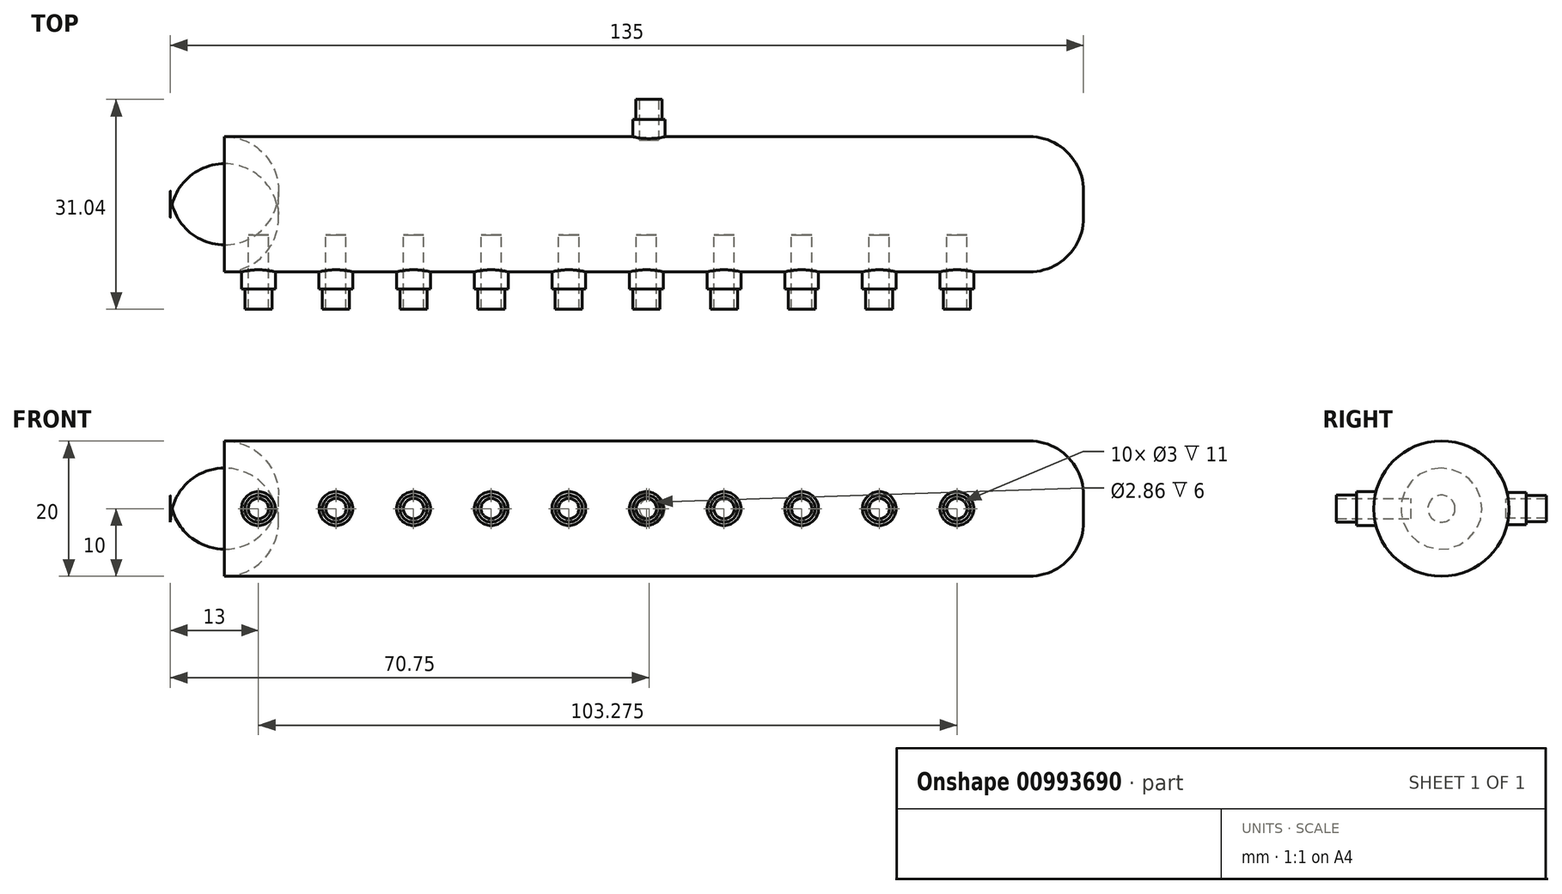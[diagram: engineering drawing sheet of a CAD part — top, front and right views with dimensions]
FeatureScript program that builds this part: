
annotation { "Feature Type Name" : "Feature", "Feature Type Description" : "" }
export const myFeature = defineFeature(function(context is Context, id is Id, definition is map)
    precondition{}
    {
        {
            assignVariable(context, id + "F0", {"name" : "big_radius", "anyValue" : 20});
        }
        {
            assignVariable(context, id + "F1", {"name" : "tube_length", "anyValue" : 135});
        }
        {
            var Q0;
            Q0=qCreatedBy(makeId("Right.planeOp"),FACE);
            var sketch = newSketch(context, id + "F2", { "sketchPlane" : qUnion([Q0])});
            skCircle(sketch, "E0", {"center": v(0, 0) * mm, "radius": 10 * mm});
            skLineSegment(sketch, "E1", {"start": v(-10, 0) * mm, "end": v(-10, 26.48) * mm, "construction": true});
            skSolve(sketch);
        }
        {
            var Q0;
            Q0=makeQuery(id+"F2.imprint","IMPRINT",FACE,{"disambiguationData":[TD([[makeQuery(id+"F2.imprint","IMPRINT",EDGE,{"derivedFrom":sQuery(id+"F2.wireOp",EDGE,"E0")}),1.0]])]});
            extrude(context, id + "F3", {"entities" : qUnion([Q0]), "depth" : (getVariable(context, 'tube_length')) * mm, "offsetDistance" : 25 * mm});
        }
        {
            var Q0;
            Q0=makeQuery(id+"F3.opExtrude","CAP_FACE",FACE,{"disambiguationData":[OSD([sQuery(id+"F2.wireOp",EDGE,"E0")])],"isStart":false});
            fillet(context, id + "F4", {"entities" : qUnion([Q0]), "radius" : 8 * mm, "tangentPropagation" : true, "allowEdgeOverflow" : false});
        }
        {
            var Q0;
            Q0=makeQuery(id+"F3.opExtrude","CAP_FACE",FACE,{"disambiguationData":[OSD([sQuery(id+"F2.wireOp",EDGE,"E0")])],"isStart":true});
            fillet(context, id + "F5", {"entities" : qUnion([Q0]), "radius" : 8 * mm, "tangentPropagation" : true, "allowEdgeOverflow" : false});
        }
        {
            var Q0;
            Q0=qCreatedBy(makeId("Front.planeOp"),FACE);
            cPlane(context, id + "F6", {"entities" : qUnion([Q0]), "cplaneType" : CPlaneType.OFFSET, "offset" : (getVariable(context, 'big_radius') / 2.1) * mm, "width" : 150 * mm, "height" : 150 * mm});
        }
        {
            var Q0;
            Q0=qCreatedBy(id+"F6.planeOp",FACE);
            var sketch = newSketch(context, id + "F7", { "sketchPlane" : qUnion([Q0])});
            skCircle(sketch, "E2", {"center": v(13, 0) * mm, "radius": 2.5 * mm});
            skCircle(sketch, "E3.0", {"center": v(13, 0) * mm, "radius": 1.5 * mm});
            skCircle(sketch, "E4.1.0.0", {"center": v(24.48, 0) * mm, "radius": 1.5 * mm});
            skCircle(sketch, "E4.1.0.1", {"center": v(24.48, 0) * mm, "radius": 2.5 * mm});
            skCircle(sketch, "E4.2.0.0", {"center": v(35.95, 0) * mm, "radius": 1.5 * mm});
            skCircle(sketch, "E4.2.0.1", {"center": v(35.95, 0) * mm, "radius": 2.5 * mm});
            skCircle(sketch, "E4.3.0.0", {"center": v(47.43, 0) * mm, "radius": 1.5 * mm});
            skCircle(sketch, "E4.3.0.1", {"center": v(47.43, 0) * mm, "radius": 2.5 * mm});
            skCircle(sketch, "E4.4.0.0", {"center": v(58.9, 0) * mm, "radius": 1.5 * mm});
            skCircle(sketch, "E4.4.0.1", {"center": v(58.9, 0) * mm, "radius": 2.5 * mm});
            skCircle(sketch, "E4.5.0.0", {"center": v(70.38, 0) * mm, "radius": 1.5 * mm});
            skCircle(sketch, "E4.5.0.1", {"center": v(70.38, 0) * mm, "radius": 2.5 * mm});
            skCircle(sketch, "E4.6.0.0", {"center": v(81.85, 0) * mm, "radius": 1.5 * mm});
            skCircle(sketch, "E4.6.0.1", {"center": v(81.85, 0) * mm, "radius": 2.5 * mm});
            skCircle(sketch, "E4.7.0.0", {"center": v(93.33, 0) * mm, "radius": 1.5 * mm});
            skCircle(sketch, "E4.7.0.1", {"center": v(93.33, 0) * mm, "radius": 2.5 * mm});
            skCircle(sketch, "E4.8.0.0", {"center": v(104.8, 0) * mm, "radius": 1.5 * mm});
            skCircle(sketch, "E4.8.0.1", {"center": v(104.8, 0) * mm, "radius": 2.5 * mm});
            skCircle(sketch, "E4.9.0.0", {"center": v(116.28, 0) * mm, "radius": 1.5 * mm});
            skCircle(sketch, "E4.9.0.1", {"center": v(116.28, 0) * mm, "radius": 2.5 * mm});
            skLineSegment(sketch, "E4.direction1", {"start": v(13, 0) * mm, "end": v(24.48, 0) * mm, "construction": true});
            skSolve(sketch);
        }
        {
            var Q0;
            Q0=makeQuery(id+"F7.imprint","IMPRINT",FACE,{"disambiguationData":[TD([[makeQuery(id+"F7.imprint","IMPRINT",EDGE,{"derivedFrom":sQuery(id+"F7.wireOp",EDGE,"E2")}),1.0]])]});
            var Q1;
            Q1=makeQuery(id+"F7.imprint","IMPRINT",FACE,{"disambiguationData":[TD([[makeQuery(id+"F7.imprint","IMPRINT",EDGE,{"derivedFrom":sQuery(id+"F7.wireOp",EDGE,"E4.1.0.0")}),-1.0]])]});
            var Q2;
            Q2=makeQuery(id+"F7.imprint","IMPRINT",FACE,{"disambiguationData":[TD([[makeQuery(id+"F7.imprint","IMPRINT",EDGE,{"derivedFrom":sQuery(id+"F7.wireOp",EDGE,"E4.2.0.0")}),-1.0]])]});
            var Q3;
            Q3=makeQuery(id+"F7.imprint","IMPRINT",FACE,{"disambiguationData":[TD([[makeQuery(id+"F7.imprint","IMPRINT",EDGE,{"derivedFrom":sQuery(id+"F7.wireOp",EDGE,"E4.3.0.0")}),-1.0]])]});
            var Q4;
            Q4=makeQuery(id+"F7.imprint","IMPRINT",FACE,{"disambiguationData":[TD([[makeQuery(id+"F7.imprint","IMPRINT",EDGE,{"derivedFrom":sQuery(id+"F7.wireOp",EDGE,"E4.4.0.0")}),-1.0]])]});
            var Q5;
            Q5=makeQuery(id+"F7.imprint","IMPRINT",FACE,{"disambiguationData":[TD([[makeQuery(id+"F7.imprint","IMPRINT",EDGE,{"derivedFrom":sQuery(id+"F7.wireOp",EDGE,"E4.5.0.0")}),-1.0]])]});
            var Q6;
            Q6=makeQuery(id+"F7.imprint","IMPRINT",FACE,{"disambiguationData":[TD([[makeQuery(id+"F7.imprint","IMPRINT",EDGE,{"derivedFrom":sQuery(id+"F7.wireOp",EDGE,"E4.6.0.0")}),-1.0]])]});
            var Q7;
            Q7=makeQuery(id+"F7.imprint","IMPRINT",FACE,{"disambiguationData":[TD([[makeQuery(id+"F7.imprint","IMPRINT",EDGE,{"derivedFrom":sQuery(id+"F7.wireOp",EDGE,"E4.7.0.0")}),-1.0]])]});
            var Q8;
            Q8=makeQuery(id+"F7.imprint","IMPRINT",FACE,{"disambiguationData":[TD([[makeQuery(id+"F7.imprint","IMPRINT",EDGE,{"derivedFrom":sQuery(id+"F7.wireOp",EDGE,"E4.8.0.0")}),-1.0]])]});
            var Q9;
            Q9=makeQuery(id+"F7.imprint","IMPRINT",FACE,{"disambiguationData":[TD([[makeQuery(id+"F7.imprint","IMPRINT",EDGE,{"derivedFrom":sQuery(id+"F7.wireOp",EDGE,"E4.9.0.0")}),-1.0]])]});
            extrude(context, id + "F8", {"entities" : qUnion([Q0, Q1, Q2, Q3, Q4, Q5, Q6, Q7, Q8, Q9]), "operationType" : NewBodyOperationType.ADD, "depth" : 3 * mm, "offsetDistance" : 25 * mm});
        }
        {
            var Q0;
            Q0=makeQuery(id+"F7.imprint","IMPRINT",FACE,{"disambiguationData":[TD([[makeQuery(id+"F7.imprint","IMPRINT",EDGE,{"derivedFrom":sQuery(id+"F7.wireOp",EDGE,"E3.0")}),1.0]])]});
            var Q1;
            Q1=makeQuery(id+"F7.imprint","IMPRINT",FACE,{"disambiguationData":[TD([[makeQuery(id+"F7.imprint","IMPRINT",EDGE,{"derivedFrom":sQuery(id+"F7.wireOp",EDGE,"E4.1.0.0")}),1.0]])]});
            var Q2;
            Q2=makeQuery(id+"F7.imprint","IMPRINT",FACE,{"disambiguationData":[TD([[makeQuery(id+"F7.imprint","IMPRINT",EDGE,{"derivedFrom":sQuery(id+"F7.wireOp",EDGE,"E4.2.0.0")}),1.0]])]});
            var Q3;
            Q3=makeQuery(id+"F7.imprint","IMPRINT",FACE,{"disambiguationData":[TD([[makeQuery(id+"F7.imprint","IMPRINT",EDGE,{"derivedFrom":sQuery(id+"F7.wireOp",EDGE,"E4.3.0.0")}),1.0]])]});
            var Q4;
            Q4=makeQuery(id+"F7.imprint","IMPRINT",FACE,{"disambiguationData":[TD([[makeQuery(id+"F7.imprint","IMPRINT",EDGE,{"derivedFrom":sQuery(id+"F7.wireOp",EDGE,"E4.4.0.0")}),1.0]])]});
            var Q5;
            Q5=makeQuery(id+"F7.imprint","IMPRINT",FACE,{"disambiguationData":[TD([[makeQuery(id+"F7.imprint","IMPRINT",EDGE,{"derivedFrom":sQuery(id+"F7.wireOp",EDGE,"E4.5.0.0")}),1.0]])]});
            var Q6;
            Q6=makeQuery(id+"F7.imprint","IMPRINT",FACE,{"disambiguationData":[TD([[makeQuery(id+"F7.imprint","IMPRINT",EDGE,{"derivedFrom":sQuery(id+"F7.wireOp",EDGE,"E4.6.0.0")}),1.0]])]});
            var Q7;
            Q7=makeQuery(id+"F7.imprint","IMPRINT",FACE,{"disambiguationData":[TD([[makeQuery(id+"F7.imprint","IMPRINT",EDGE,{"derivedFrom":sQuery(id+"F7.wireOp",EDGE,"E4.7.0.0")}),1.0]])]});
            var Q8;
            Q8=makeQuery(id+"F7.imprint","IMPRINT",FACE,{"disambiguationData":[TD([[makeQuery(id+"F7.imprint","IMPRINT",EDGE,{"derivedFrom":sQuery(id+"F7.wireOp",EDGE,"E4.8.0.0")}),1.0]])]});
            var Q9;
            Q9=makeQuery(id+"F7.imprint","IMPRINT",FACE,{"disambiguationData":[TD([[makeQuery(id+"F7.imprint","IMPRINT",EDGE,{"derivedFrom":sQuery(id+"F7.wireOp",EDGE,"E4.9.0.0")}),1.0]])]});
            extrude(context, id + "F9", {"entities" : qUnion([Q0, Q1, Q2, Q3, Q4, Q5, Q6, Q7, Q8, Q9]), "operationType" : NewBodyOperationType.REMOVE, "endBound" : BoundingType.SYMMETRIC, "oppositeDirection" : true, "depth" : 10 * mm, "offsetDistance" : 25 * mm});
        }
        {
            var Q0;
            Q0=qCreatedBy(makeId("Front.planeOp"),FACE);
            cPlane(context, id + "F10", {"entities" : qUnion([Q0]), "cplaneType" : CPlaneType.OFFSET, "offset" : (getVariable(context, 'big_radius') / 2.1) * mm, "oppositeDirection" : true, "width" : 150 * mm, "height" : 150 * mm});
        }
        {
            var Q0;
            Q0=qCreatedBy(id+"F10.planeOp",FACE);
            var sketch = newSketch(context, id + "F11", { "sketchPlane" : qUnion([Q0])});
            skCircle(sketch, "E5.0", {"center": v(70.75, 0) * mm, "radius": 2.38 * mm});
            skCircle(sketch, "E5.1", {"center": v(70.75, 0) * mm, "radius": 1.43 * mm});
            skSolve(sketch);
        }
        {
            var Q0;
            Q0=makeQuery(id+"F11.imprint","IMPRINT",FACE,{"disambiguationData":[TD([[makeQuery(id+"F11.imprint","IMPRINT",EDGE,{"derivedFrom":sQuery(id+"F11.wireOp",EDGE,"E5.1")}),1.0]])]});
            extrude(context, id + "F12", {"entities" : qUnion([Q0]), "operationType" : NewBodyOperationType.REMOVE, "oppositeDirection" : true, "depth" : 10 * mm, "offsetDistance" : 25 * mm});
        }
        {
            var Q0;
            Q0=makeQuery(id+"F11.imprint","IMPRINT",FACE,{"disambiguationData":[TD([[makeQuery(id+"F11.imprint","IMPRINT",EDGE,{"derivedFrom":sQuery(id+"F11.wireOp",EDGE,"E5.0")}),1.0]])]});
            extrude(context, id + "F13", {"entities" : qUnion([Q0]), "operationType" : NewBodyOperationType.ADD, "oppositeDirection" : true, "depth" : 3 * mm, "offsetDistance" : 25 * mm});
        }
        {
            var Q0;
            Q0=makeQuery(id+"F8.opExtrude","CAP_FACE",FACE,{"disambiguationData":[OSD([sQuery(id+"F7.wireOp",EDGE,"E2"),sQuery(id+"F7.wireOp",EDGE,"E3.0")])],"isStart":false});
            var sketch = newSketch(context, id + "F14", { "sketchPlane" : qUnion([Q0])});
            skCircle(sketch, "E6.0", {"center": v(13, 0) * mm, "radius": 1.5 * mm});
            skCircle(sketch, "E7.0", {"center": v(13, 0) * mm, "radius": 2 * mm});
            skCircle(sketch, "E8.1.0.0", {"center": v(24.47, 0) * mm, "radius": 1.5 * mm});
            skCircle(sketch, "E8.1.0.1", {"center": v(24.47, 0) * mm, "radius": 2 * mm});
            skCircle(sketch, "E8.2.0.0", {"center": v(35.95, 0) * mm, "radius": 1.5 * mm});
            skCircle(sketch, "E8.2.0.1", {"center": v(35.95, 0) * mm, "radius": 2 * mm});
            skCircle(sketch, "E8.3.0.0", {"center": v(47.42, 0) * mm, "radius": 1.5 * mm});
            skCircle(sketch, "E8.3.0.1", {"center": v(47.42, 0) * mm, "radius": 2 * mm});
            skCircle(sketch, "E8.4.0.0", {"center": v(58.9, 0) * mm, "radius": 1.5 * mm});
            skCircle(sketch, "E8.4.0.1", {"center": v(58.9, 0) * mm, "radius": 2 * mm});
            skCircle(sketch, "E8.5.0.0", {"center": v(70.38, 0) * mm, "radius": 1.5 * mm});
            skCircle(sketch, "E8.5.0.1", {"center": v(70.38, 0) * mm, "radius": 2 * mm});
            skCircle(sketch, "E8.6.0.0", {"center": v(81.85, 0) * mm, "radius": 1.5 * mm});
            skCircle(sketch, "E8.6.0.1", {"center": v(81.85, 0) * mm, "radius": 2 * mm});
            skCircle(sketch, "E8.7.0.0", {"center": v(93.32, 0) * mm, "radius": 1.5 * mm});
            skCircle(sketch, "E8.7.0.1", {"center": v(93.32, 0) * mm, "radius": 2 * mm});
            skCircle(sketch, "E8.8.0.0", {"center": v(104.8, 0) * mm, "radius": 1.5 * mm});
            skCircle(sketch, "E8.8.0.1", {"center": v(104.8, 0) * mm, "radius": 2 * mm});
            skCircle(sketch, "E8.9.0.0", {"center": v(116.27, 0) * mm, "radius": 1.5 * mm});
            skCircle(sketch, "E8.9.0.1", {"center": v(116.27, 0) * mm, "radius": 2 * mm});
            skLineSegment(sketch, "E8.direction1", {"start": v(13, 0) * mm, "end": v(24.47, 0) * mm, "construction": true});
            skSolve(sketch);
        }
        {
            var Q0;
            Q0=makeQuery(id+"F14.imprint","IMPRINT",FACE,{"disambiguationData":[TD([[makeQuery(id+"F14.imprint","IMPRINT",EDGE,{"derivedFrom":sQuery(id+"F14.wireOp",EDGE,"E6.0")}),-1.0]])]});
            var Q1;
            Q1=makeQuery(id+"F14.imprint","IMPRINT",FACE,{"disambiguationData":[TD([[makeQuery(id+"F14.imprint","IMPRINT",EDGE,{"derivedFrom":sQuery(id+"F14.wireOp",EDGE,"E8.1.0.0")}),-1.0]])]});
            var Q2;
            Q2=makeQuery(id+"F14.imprint","IMPRINT",FACE,{"disambiguationData":[TD([[makeQuery(id+"F14.imprint","IMPRINT",EDGE,{"derivedFrom":sQuery(id+"F14.wireOp",EDGE,"E8.2.0.0")}),-1.0]])]});
            var Q3;
            Q3=makeQuery(id+"F14.imprint","IMPRINT",FACE,{"disambiguationData":[TD([[makeQuery(id+"F14.imprint","IMPRINT",EDGE,{"derivedFrom":sQuery(id+"F14.wireOp",EDGE,"E8.3.0.0")}),-1.0]])]});
            var Q4;
            Q4=makeQuery(id+"F14.imprint","IMPRINT",FACE,{"disambiguationData":[TD([[makeQuery(id+"F14.imprint","IMPRINT",EDGE,{"derivedFrom":sQuery(id+"F14.wireOp",EDGE,"E8.4.0.0")}),-1.0]])]});
            var Q5;
            Q5=makeQuery(id+"F14.imprint","IMPRINT",FACE,{"disambiguationData":[TD([[makeQuery(id+"F14.imprint","IMPRINT",EDGE,{"derivedFrom":sQuery(id+"F14.wireOp",EDGE,"E8.5.0.0")}),-1.0]])]});
            var Q6;
            Q6=makeQuery(id+"F14.imprint","IMPRINT",FACE,{"disambiguationData":[TD([[makeQuery(id+"F14.imprint","IMPRINT",EDGE,{"derivedFrom":sQuery(id+"F14.wireOp",EDGE,"E8.6.0.0")}),-1.0]])]});
            var Q7;
            Q7=makeQuery(id+"F14.imprint","IMPRINT",FACE,{"disambiguationData":[TD([[makeQuery(id+"F14.imprint","IMPRINT",EDGE,{"derivedFrom":sQuery(id+"F14.wireOp",EDGE,"E8.7.0.0")}),-1.0]])]});
            var Q8;
            Q8=makeQuery(id+"F14.imprint","IMPRINT",FACE,{"disambiguationData":[TD([[makeQuery(id+"F14.imprint","IMPRINT",EDGE,{"derivedFrom":sQuery(id+"F14.wireOp",EDGE,"E8.8.0.0")}),-1.0]])]});
            var Q9;
            Q9=makeQuery(id+"F14.imprint","IMPRINT",FACE,{"disambiguationData":[TD([[makeQuery(id+"F14.imprint","IMPRINT",EDGE,{"derivedFrom":sQuery(id+"F14.wireOp",EDGE,"E8.9.0.0")}),-1.0]])]});
            extrude(context, id + "F15", {"entities" : qUnion([Q0, Q1, Q2, Q3, Q4, Q5, Q6, Q7, Q8, Q9]), "operationType" : NewBodyOperationType.ADD, "depth" : 3 * mm, "offsetDistance" : 25 * mm});
        }
        {
            var Q0;
            Q0=makeQuery(id+"F13.opExtrude","CAP_FACE",FACE,{"disambiguationData":[OSD([sQuery(id+"F11.wireOp",EDGE,"E5.0"),sQuery(id+"F11.wireOp",EDGE,"E5.1")])],"isStart":false});
            var sketch = newSketch(context, id + "F16", { "sketchPlane" : qUnion([Q0])});
            skCircle(sketch, "E9.0", {"center": v(-70.75, 0) * mm, "radius": 1.43 * mm});
            skCircle(sketch, "E10.0", {"center": v(-70.75, 0) * mm, "radius": 1.93 * mm});
            skSolve(sketch);
        }
        {
            var Q0;
            Q0=makeQuery(id+"F16.imprint","IMPRINT",FACE,{"disambiguationData":[TD([[makeQuery(id+"F16.imprint","IMPRINT",EDGE,{"derivedFrom":sQuery(id+"F16.wireOp",EDGE,"E9.0")}),1.0]])]});
            extrude(context, id + "F17", {"entities" : qUnion([Q0]), "operationType" : NewBodyOperationType.ADD, "depth" : 3 * mm, "offsetDistance" : 25 * mm});
        }
    });
